# Revit family: Towel Ring- Trendly Hotels- Gala - 53071
name_source: partatom
category: Plumbing Fixtures
units: mm (PartAtom-declared; Revit-internal decimal feet)

## family parameters
Cut with Voids When Loaded = No
Host = Face
OmniClass Number = 23.45.05.00
OmniClass Title = Sanitary Equipment
Part Type = Normal
Room Calculation Point = No
Round Connector Dimension = Use Diameter
Shared = No

## types (1)
- 5307100 Chrome
    BIMobject category = Bathroom Accessories
    Date of publishing = 2015-05-01
    Default Elevation = 1219 mm
    Description = Towel ring
    Design country = Spain
    Edition number = 1
    IFC Classification = Object
    Manufacturer URL = http://www.gala.es
    Manufacturer country = Spain
    Manufacturer name = GALA
    Model = 53071
    Nominal height = 220
    Nominal width = 200
    Primary Material = Chrome- Trendly Hotels - Gala
    Product Guid = 4c1dca54-f27a-4a78-8d14-a200a19dd9cd
    Product SKU = 5307100
    Product data url = http://bimobject.com
    Product family = Trendly hotels
    Product group = Bathroom accesories
    QR code = http://bimobject.com
    Technical description = http://www.gala.es
    URL = http://www.gala.es
    Uniclass 1.4 Code = L824
    Uniclass 1.4 Description = Bathroom, toilet furniture and fittings
    Weight Net (Kg) = 0

## geometry (parser evidence)
native form markers: Sweep x4
no freeform markers — native parametric forms only
